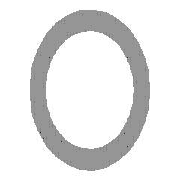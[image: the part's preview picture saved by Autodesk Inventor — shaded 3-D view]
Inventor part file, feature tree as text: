
AUTODESK INVENTOR PART (.ipt)
format: ipt  version: 2013 (Build 170138000, 138)  size: 108,544 bytes
history: native  units: mm (DEFAULTED — no unit token found)
features: other x3, sketch x3, plane x1
ambient origin geometry x8: Origin, YZ Plane, XZ Plane, XY Plane, X Axis, Y Axis, Z Axis, Center Point
bodies: Solid1 (feature_tree), Body (feature_tree)
feature tree (7):
  other  "Driven Length"
  other  "Start plane"
  other  "End plane"
  sketch  "Sketch1"  dims[d0=21.336mm]
  sketch  "Sketch2"  dims[d1=2.7686mm]
  plane  "Work Plane3"
  sketch  "Sketch3"  dims[d2=609.6mm d3=0.0mm d5=-0.0mm d6=609.6mm d7=90.0deg d8=609.6mm]
